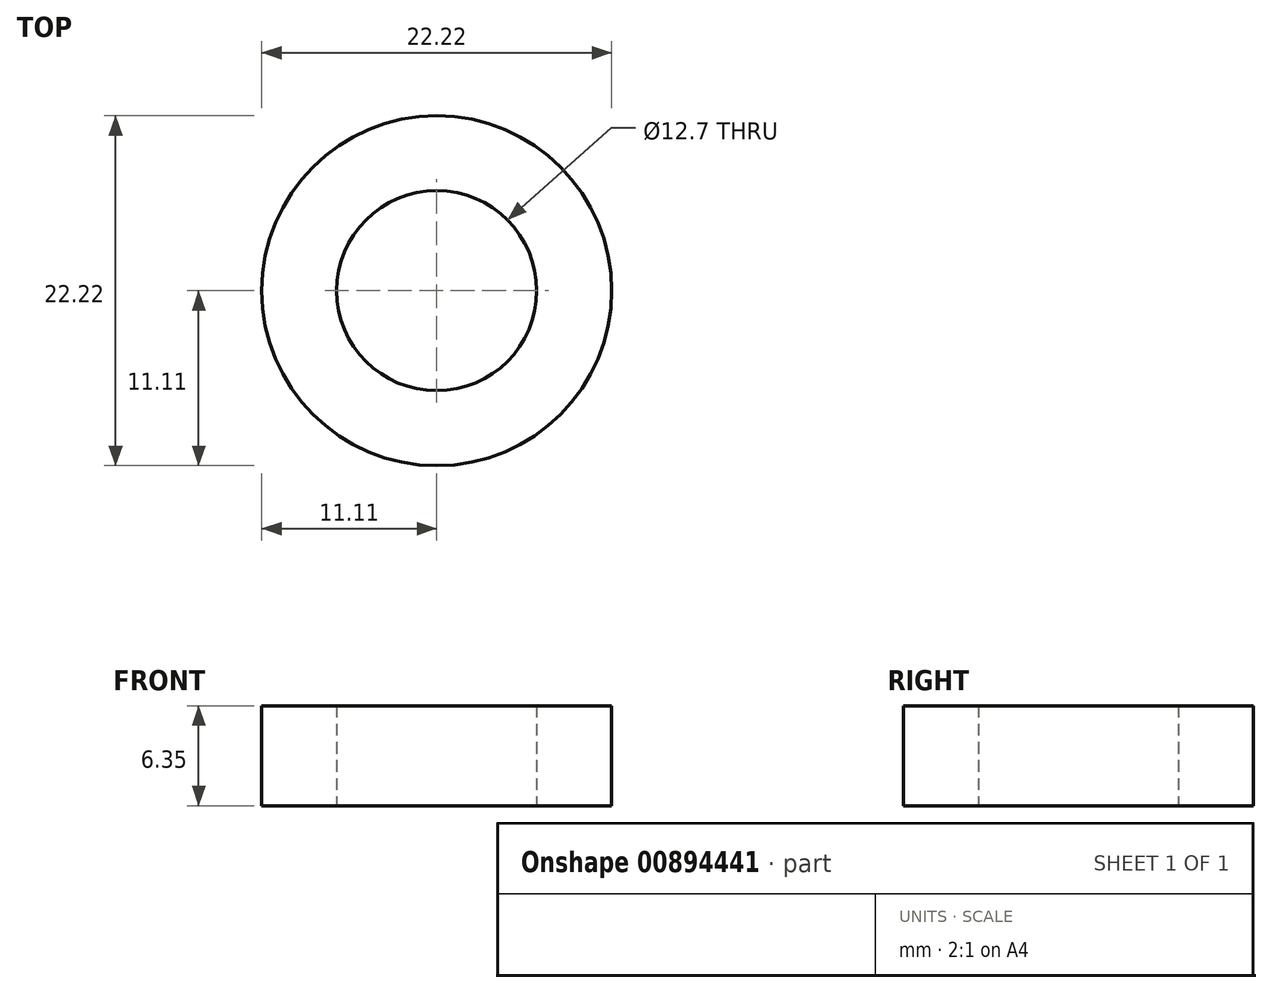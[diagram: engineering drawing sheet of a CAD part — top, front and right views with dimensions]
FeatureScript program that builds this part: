
annotation { "Feature Type Name" : "Feature", "Feature Type Description" : "" }
export const myFeature = defineFeature(function(context is Context, id is Id, definition is map)
    precondition{}
    {
        {
            var Q0;
            Q0=qCreatedBy(makeId("Top.planeOp"),FACE);
            var sketch = newSketch(context, id + "F0", { "sketchPlane" : qUnion([Q0])});
            skCircle(sketch, "E0", {"center": v(0, 0) * mm, "radius": 6.35 * mm});
            skCircle(sketch, "E1", {"center": v(0, 0) * mm, "radius": 11.11 * mm});
            skSolve(sketch);
        }
        {
            var Q0;
            Q0=makeQuery(id+"F0.imprint","IMPRINT",FACE,{"disambiguationData":[TD([[makeQuery(id+"F0.imprint","IMPRINT",EDGE,{"derivedFrom":sQuery(id+"F0.wireOp",EDGE,"E0")}),-1.0]])]});
            extrude(context, id + "F1", {"entities" : qUnion([Q0]), "depth" : 6.35 * mm, "offsetDistance" : 25.4 * mm});
        }
    });
